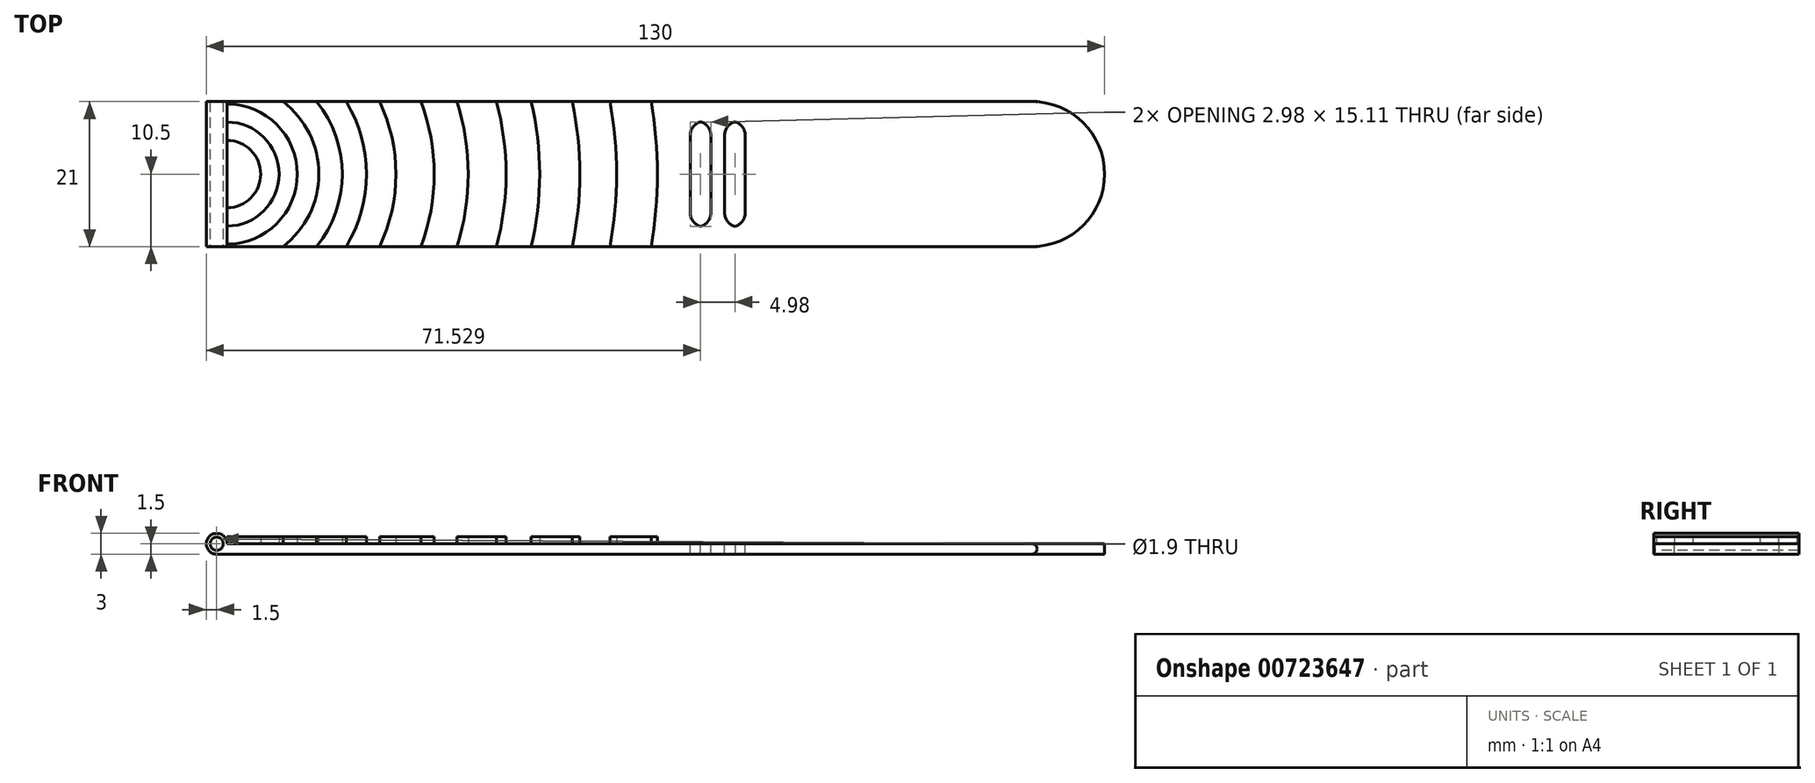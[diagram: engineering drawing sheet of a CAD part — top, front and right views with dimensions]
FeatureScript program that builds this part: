
annotation { "Feature Type Name" : "Feature", "Feature Type Description" : "" }
export const myFeature = defineFeature(function(context is Context, id is Id, definition is map)
    precondition{}
    {
        {
            var Q0;
            Q0=qCreatedBy(makeId("Front.planeOp"),FACE);
            var sketch = newSketch(context, id + "F0", { "sketchPlane" : qUnion([Q0])});
            skCircle(sketch, "E0", {"center": v(0, 0) * mm, "radius": 1.5 * mm});
            skLineSegment(sketch, "E1", {"start": v(0, -1.5) * mm, "end": v(118, -1.5) * mm});
            skLineSegment(sketch, "E2", {"start": v(118, 0) * mm, "end": v(1.5, 0) * mm});
            skArc(sketch, "E3", {"start": v(118, -1.5) * mm, "mid": v(118.75, -0.75) * mm, "end": v(118, 0) * mm});
            skSolve(sketch);
        }
        {
            var Q0;
            Q0 = qSketchRegion(id + "F0", true);
            extrude(context, id + "F1", {"entities" : qUnion([Q0]), "oppositeDirection" : true, "depth" : 21 * mm, "offsetDistance" : 25.4 * mm});
        }
        {
            var Q0;
            Q0=makeQuery(id+"F1.opExtrude","SWEPT_FACE",FACE,{"disambiguationData":[OSD([sQuery(id+"F0.wireOp",EDGE,"E1")])]});
            var sketch = newSketch(context, id + "F2", { "sketchPlane" : qUnion([Q0])});
            skArc(sketch, "E4", {"start": v(118, -21) * mm, "mid": v(128.5, -10.5) * mm, "end": v(118, 0) * mm});
            skSolve(sketch);
        }
        {
            var Q0;
            Q0=makeQuery(id+"F2.imprint","IMPRINT",FACE,{"disambiguationData":[TD([[makeQuery(id+"F2.imprint","IMPRINT",EDGE,{"derivedFrom":sQuery(id+"F2.wireOp",EDGE,"E4")}),1.0]])]});
            extrude(context, id + "F3", {"entities" : qUnion([Q0]), "operationType" : NewBodyOperationType.ADD, "oppositeDirection" : true, "depth" : 1.5 * mm, "offsetDistance" : 25.4 * mm});
        }
        {
            var Q0;
            Q0=makeQuery(id+"F1.opExtrude","CAP_FACE",FACE,{"disambiguationData":[OSD([sQuery(id+"F0.wireOp",EDGE,"E0"),sQuery(id+"F0.wireOp",EDGE,"E1"),sQuery(id+"F0.wireOp",EDGE,"E2"),sQuery(id+"F0.wireOp",EDGE,"E3")])],"isStart":true});
            var sketch = newSketch(context, id + "F4", { "sketchPlane" : qUnion([Q0])});
            skCircle(sketch, "E5", {"center": v(0, 0) * mm, "radius": 0.95 * mm});
            skSolve(sketch);
        }
        {
            var Q0;
            Q0 = qSketchRegion(id + "F4", true);
            extrude(context, id + "F5", {"entities" : qUnion([Q0]), "operationType" : NewBodyOperationType.REMOVE, "oppositeDirection" : true, "depth" : 25.4 * mm, "offsetDistance" : 25.4 * mm});
        }
        {
            var Q0;
            Q0=makeQuery(id+"F3.boolean.opBoolean","MERGE",FACE,{"derivedFrom":[makeQuery(id+"F1.opExtrude","SWEPT_FACE",FACE,{"disambiguationData":[OSD([sQuery(id+"F0.wireOp",EDGE,"E2")])]}),makeQuery(id+"F3.opExtrude","CAP_FACE",FACE,{"disambiguationData":[OSD([sQuery(id+"F0.wireOp",EDGE,"E1"),sQuery(id+"F0.wireOp",EDGE,"E3"),sQuery(id+"F2.wireOp",EDGE,"E4")])],"isStart":false})]});
            var sketch = newSketch(context, id + "F6", { "sketchPlane" : qUnion([Q0])});
            skLineSegment(sketch, "E6.bottom", {"start": v(76.5, 18.12) * mm, "end": v(73.52, 18.12) * mm});
            skLineSegment(sketch, "E6.top", {"start": v(76.5, 2.88) * mm, "end": v(73.52, 2.88) * mm});
            skLineSegment(sketch, "E6.left", {"start": v(76.5, 18.12) * mm, "end": v(76.5, 2.88) * mm});
            skLineSegment(sketch, "E6.right", {"start": v(73.52, 18.12) * mm, "end": v(73.52, 2.88) * mm});
            skPoint(sketch, "E6.middle", {"position": v(75, 10.5) * mm});
            skPoint(sketch, "E6.middle.positionSnap0", {"position": v(1.5, 10.5) * mm});
            skPoint(sketch, "E6.centerSnap0", {"position": v(1.5, 10.5) * mm});
            skLineSegment(sketch, "E7.bottom", {"start": v(71.52, 18.12) * mm, "end": v(68.54, 18.12) * mm});
            skLineSegment(sketch, "E7.top", {"start": v(71.52, 2.88) * mm, "end": v(68.54, 2.88) * mm});
            skLineSegment(sketch, "E7.left", {"start": v(71.52, 18.12) * mm, "end": v(71.52, 2.88) * mm});
            skLineSegment(sketch, "E7.right", {"start": v(68.54, 18.12) * mm, "end": v(68.54, 2.88) * mm});
            skPoint(sketch, "E7.middle", {"position": v(70.03, 10.5) * mm});
            skSolve(sketch);
        }
        {
            var Q0;
            Q0=makeQuery(id+"F6.imprint","IMPRINT",FACE,{"disambiguationData":[TD([[makeQuery(id+"F6.imprint","IMPRINT",EDGE,{"derivedFrom":sQuery(id+"F6.wireOp",EDGE,"E7.bottom")}),1.0]])]});
            var Q1;
            Q1=makeQuery(id+"F6.imprint","IMPRINT",FACE,{"disambiguationData":[TD([[makeQuery(id+"F6.imprint","IMPRINT",EDGE,{"derivedFrom":sQuery(id+"F6.wireOp",EDGE,"E6.bottom")}),1.0]])]});
            extrude(context, id + "F7", {"entities" : qUnion([Q0, Q1]), "operationType" : NewBodyOperationType.REMOVE, "oppositeDirection" : true, "depth" : 25.4 * mm, "offsetDistance" : 25.4 * mm});
        }
        {
            var Q0;
            Q0=makeQuery(id+"F7.boolean.opBoolean","COPY",EDGE,{"derivedFrom":makeQuery(id+"F7.opExtrude","SWEPT_EDGE",EDGE,{"disambiguationData":[OSD([sQuery(id+"F6.wireOp",EDGE,"E7.top"),sQuery(id+"F6.wireOp",EDGE,"E7.right")])]})});
            var Q1;
            Q1=makeQuery(id+"F7.boolean.opBoolean","COPY",EDGE,{"derivedFrom":makeQuery(id+"F7.opExtrude","SWEPT_EDGE",EDGE,{"disambiguationData":[OSD([sQuery(id+"F6.wireOp",EDGE,"E7.bottom"),sQuery(id+"F6.wireOp",EDGE,"E7.right")])]})});
            var Q2;
            Q2=makeQuery(id+"F7.boolean.opBoolean","COPY",EDGE,{"derivedFrom":makeQuery(id+"F7.opExtrude","SWEPT_EDGE",EDGE,{"disambiguationData":[OSD([sQuery(id+"F6.wireOp",EDGE,"E7.bottom"),sQuery(id+"F6.wireOp",EDGE,"E7.left")])]})});
            var Q3;
            Q3=makeQuery(id+"F7.boolean.opBoolean","COPY",EDGE,{"derivedFrom":makeQuery(id+"F7.opExtrude","SWEPT_EDGE",EDGE,{"disambiguationData":[OSD([sQuery(id+"F6.wireOp",EDGE,"E7.top"),sQuery(id+"F6.wireOp",EDGE,"E7.left")])]})});
            fillet(context, id + "F8", {"entities" : qUnion([Q0, Q1, Q2, Q3]), "radius" : 2 * mm, "tangentPropagation" : true, "allowEdgeOverflow" : false});
        }
        {
            var Q0;
            Q0=makeQuery(id+"F7.boolean.opBoolean","COPY",EDGE,{"derivedFrom":makeQuery(id+"F7.opExtrude","SWEPT_EDGE",EDGE,{"disambiguationData":[OSD([sQuery(id+"F6.wireOp",EDGE,"E6.bottom"),sQuery(id+"F6.wireOp",EDGE,"E6.right")])]})});
            var Q1;
            Q1=makeQuery(id+"F7.boolean.opBoolean","COPY",EDGE,{"derivedFrom":makeQuery(id+"F7.opExtrude","SWEPT_EDGE",EDGE,{"disambiguationData":[OSD([sQuery(id+"F6.wireOp",EDGE,"E6.top"),sQuery(id+"F6.wireOp",EDGE,"E6.right")])]})});
            var Q2;
            Q2=makeQuery(id+"F7.boolean.opBoolean","COPY",EDGE,{"derivedFrom":makeQuery(id+"F7.opExtrude","SWEPT_EDGE",EDGE,{"disambiguationData":[OSD([sQuery(id+"F6.wireOp",EDGE,"E6.top"),sQuery(id+"F6.wireOp",EDGE,"E6.left")])]})});
            var Q3;
            Q3=makeQuery(id+"F7.boolean.opBoolean","COPY",EDGE,{"derivedFrom":makeQuery(id+"F7.opExtrude","SWEPT_EDGE",EDGE,{"disambiguationData":[OSD([sQuery(id+"F6.wireOp",EDGE,"E6.bottom"),sQuery(id+"F6.wireOp",EDGE,"E6.left")])]})});
            fillet(context, id + "F9", {"entities" : qUnion([Q0, Q1, Q2, Q3]), "radius" : 2 * mm, "tangentPropagation" : true, "allowEdgeOverflow" : false});
        }
        {
            var Q0;
            Q0=makeQuery(id+"F3.boolean.opBoolean","MERGE",FACE,{"derivedFrom":[makeQuery(id+"F1.opExtrude","SWEPT_FACE",FACE,{"disambiguationData":[OSD([sQuery(id+"F0.wireOp",EDGE,"E2")])]}),makeQuery(id+"F3.opExtrude","CAP_FACE",FACE,{"disambiguationData":[OSD([sQuery(id+"F0.wireOp",EDGE,"E1"),sQuery(id+"F0.wireOp",EDGE,"E3"),sQuery(id+"F2.wireOp",EDGE,"E4")])],"isStart":false})]});
            var sketch = newSketch(context, id + "F10", { "sketchPlane" : qUnion([Q0])});
            skCircle(sketch, "E8", {"center": v(1.5, 10.5) * mm, "radius": 2.57 * mm});
            skCircle(sketch, "E9", {"center": v(1.5, 10.5) * mm, "radius": 4.88 * mm});
            skCircle(sketch, "E10", {"center": v(1.5, 10.5) * mm, "radius": 7.52 * mm});
            skCircle(sketch, "E11", {"center": v(1.5, 10.5) * mm, "radius": 10.15 * mm});
            skArc(sketch, "E12", {"start": v(9.62, 0) * mm, "mid": v(14.77, 10.5) * mm, "end": v(9.62, 21) * mm});
            skArc(sketch, "E13", {"start": v(14.44, 0) * mm, "mid": v(18.17, 10.5) * mm, "end": v(14.44, 21) * mm});
            skArc(sketch, "E14", {"start": v(18.75, 0) * mm, "mid": v(21.7, 10.5) * mm, "end": v(18.75, 21) * mm});
            skArc(sketch, "E15", {"start": v(23.57, 0) * mm, "mid": v(25.94, 10.5) * mm, "end": v(23.57, 21) * mm});
            skArc(sketch, "E16", {"start": v(29.58, 0) * mm, "mid": v(31.48, 10.5) * mm, "end": v(29.58, 21) * mm});
            skArc(sketch, "E17", {"start": v(34.8, 0) * mm, "mid": v(36.4, 10.5) * mm, "end": v(34.8, 21) * mm});
            skArc(sketch, "E18", {"start": v(40.49, 0) * mm, "mid": v(41.88, 10.5) * mm, "end": v(40.49, 21) * mm});
            skArc(sketch, "E19", {"start": v(45.5, 0) * mm, "mid": v(46.74, 10.5) * mm, "end": v(45.5, 21) * mm});
            skArc(sketch, "E20", {"start": v(51.46, 0) * mm, "mid": v(52.55, 10.5) * mm, "end": v(51.46, 21) * mm});
            skArc(sketch, "E21", {"start": v(56.91, 0) * mm, "mid": v(57.9, 10.5) * mm, "end": v(56.91, 21) * mm});
            skArc(sketch, "E22", {"start": v(62.89, 0) * mm, "mid": v(63.78, 10.5) * mm, "end": v(62.89, 21) * mm});
            skLineSegment(sketch, "E23", {"start": v(1.5, 0) * mm, "end": v(62.89, 0) * mm});
            skLineSegment(sketch, "E24", {"start": v(62.89, 21) * mm, "end": v(1.5, 21) * mm});
            skSolve(sketch);
        }
        {
            var Q0;
            {var subQ0=sQuery(id+"F10.wireOp",EDGE,"E9");var subQ1=makeQuery(id+"F1.opExtrude","SWEPT_EDGE",EDGE,{"disambiguationData":[OSD([sQuery(id+"F0.wireOp",EDGE,"E0"),sQuery(id+"F0.wireOp",EDGE,"E2")])]});var subQ2=makeQuery(id+"F10.imprint","INTERSECT",VERTEX,{"disambiguationData":[OD(0.0)],"derivedFrom":[subQ1,subQ0]});Q0=makeQuery(id+"F10.imprint","IMPRINT",FACE,{"disambiguationData":[TD([[makeQuery(id+"F10.imprint","IMPRINT",EDGE,{"disambiguationData":[TD([[subQ2,-1.0]])],"derivedFrom":subQ0}),-1.0]])]});}
            var Q1;
            {var subQ3=sQuery(id+"F10.wireOp",EDGE,"E12");Q1=makeQuery(id+"F10.imprint","IMPRINT",FACE,{"disambiguationData":[TD([[makeQuery(id+"F10.imprint","IMPRINT",EDGE,{"derivedFrom":subQ3}),1.0]])]});}
            var Q2;
            {var subQ0=sQuery(id+"F10.wireOp",EDGE,"E13");Q2=makeQuery(id+"F10.imprint","IMPRINT",FACE,{"disambiguationData":[TD([[makeQuery(id+"F10.imprint","IMPRINT",EDGE,{"derivedFrom":subQ0}),-1.0]])]});}
            var Q3;
            {var subQ0=sQuery(id+"F10.wireOp",EDGE,"E15");Q3=makeQuery(id+"F10.imprint","IMPRINT",FACE,{"disambiguationData":[TD([[makeQuery(id+"F10.imprint","IMPRINT",EDGE,{"derivedFrom":subQ0}),-1.0]])]});}
            var Q4;
            {var subQ0=sQuery(id+"F10.wireOp",EDGE,"E17");Q4=makeQuery(id+"F10.imprint","IMPRINT",FACE,{"disambiguationData":[TD([[makeQuery(id+"F10.imprint","IMPRINT",EDGE,{"derivedFrom":subQ0}),-1.0]])]});}
            var Q5;
            {var subQ0=sQuery(id+"F10.wireOp",EDGE,"E19");Q5=makeQuery(id+"F10.imprint","IMPRINT",FACE,{"disambiguationData":[TD([[makeQuery(id+"F10.imprint","IMPRINT",EDGE,{"derivedFrom":subQ0}),-1.0]])]});}
            var Q6;
            {var subQ0=sQuery(id+"F10.wireOp",EDGE,"E21");Q6=makeQuery(id+"F10.imprint","IMPRINT",FACE,{"disambiguationData":[TD([[makeQuery(id+"F10.imprint","IMPRINT",EDGE,{"derivedFrom":subQ0}),-1.0]])]});}
            extrude(context, id + "F11", {"entities" : qUnion([Q0, Q1, Q2, Q3, Q4, Q5, Q6]), "depth" : 1 * mm, "offsetDistance" : 25.4 * mm});
        }
    });
